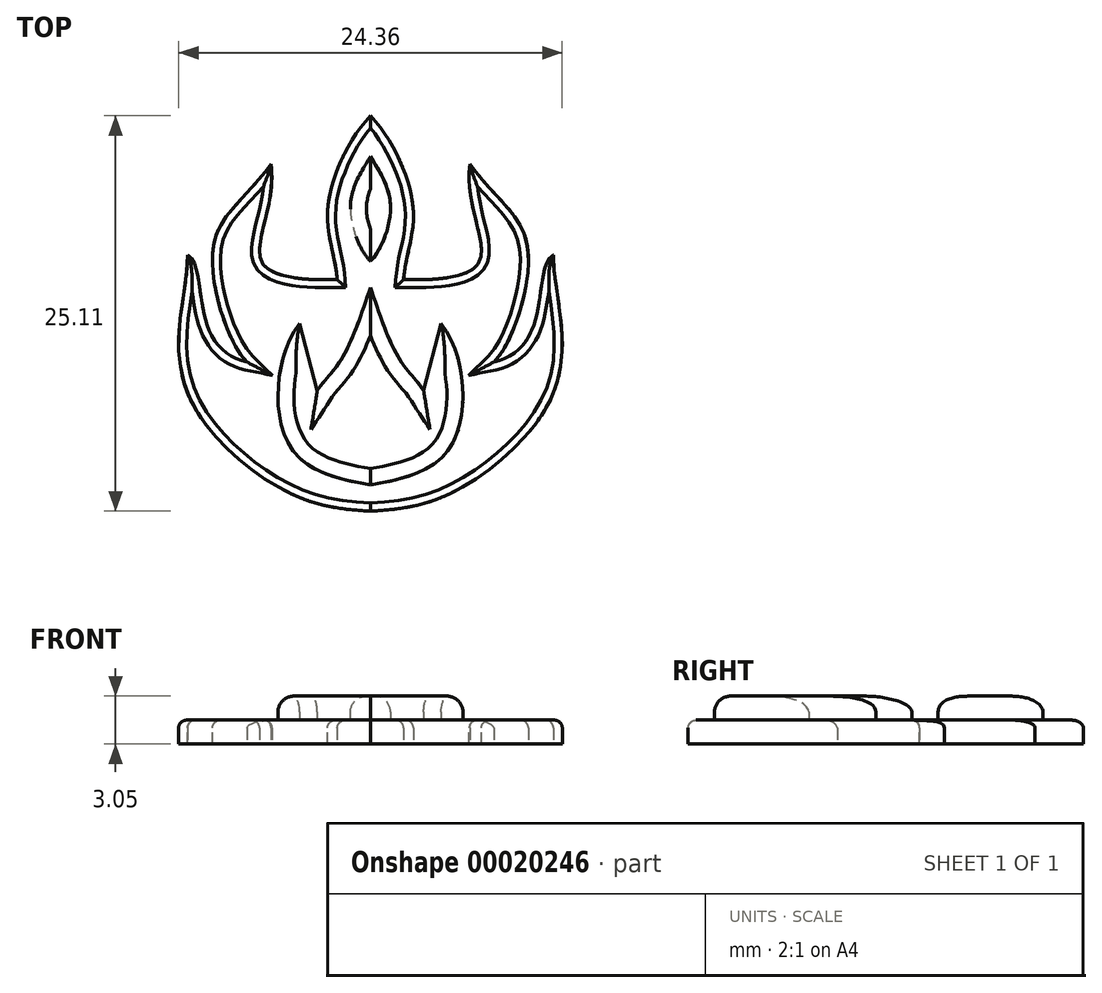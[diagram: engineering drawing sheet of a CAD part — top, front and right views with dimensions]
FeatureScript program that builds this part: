
annotation { "Feature Type Name" : "Feature", "Feature Type Description" : "" }
export const myFeature = defineFeature(function(context is Context, id is Id, definition is map)
    precondition{}
    {
        {
            var Q0;
            Q0=qCreatedBy(makeId("Top.planeOp"),FACE);
            var sketch = newSketch(context, id + "F0", { "sketchPlane" : qUnion([Q0])});
            skCircle(sketch, "E0", {"center": v(0, 0) * mm, "radius": 12.7 * mm});
            skSolve(sketch);
        }
        {
            var Q0;
            Q0=makeQuery(id+"F0.imprint","IMPRINT",FACE,{"disambiguationData":[TD([[makeQuery(id+"F0.imprint","IMPRINT",EDGE,{"derivedFrom":sQuery(id+"F0.wireOp",EDGE,"E0")}),1.0]])]});
            var Q1;
            Q1=sQuery(id+"F0.wireOp",EDGE,"E0");
            extrude(context, id + "F1", {"entities" : qUnion([Q0]), "surfaceEntities" : qUnion([Q1]), "depth" : 1.52 * mm});
        }
        {
            var Q0;
            Q0=qCreatedBy(makeId("Top.planeOp"),FACE);
            var sketch = newSketch(context, id + "F2", { "sketchPlane" : qUnion([Q0])});
            skFitSpline(sketch, "E1", {"points": [v(-6.32, 9.47) * mm, v(-9.99, 4.16) * mm, v(-7.84, -3.1) * mm], "startDerivative": vector(-11.2, -15.16) * mm, "endDerivative": vector(7.05, -6.8) * mm});
            skFitSpline(sketch, "E2", {"points": [v(0, 12.55) * mm, v(-2.72, 6.54) * mm, v(-2.1, 2.14) * mm], "startDerivative": vector(-7.74, -8.23) * mm, "endDerivative": vector(0.56, -9.4) * mm});
            skFitSpline(sketch, "E3", {"points": [v(-6.32, 9.47) * mm, v(-6.81, 3.12) * mm, v(-2.1, 2.14) * mm], "startDerivative": vector(2.17, -14.8) * mm, "endDerivative": vector(8.57, 0.21) * mm});
            skFitSpline(sketch, "E4", {"points": [v(-7.84, -3.1) * mm, v(-10.43, -0.58) * mm, v(-11.63, 3.7) * mm], "startDerivative": vector(-7.72, 1.59) * mm, "endDerivative": vector(-4.68, 1.95) * mm});
            skFitSpline(sketch, "E5", {"points": [v(-11.63, 3.7) * mm, v(-12.18, -1.7) * mm, v(-10.5, -7) * mm, v(-4.34, -11.76) * mm, v(0, -12.56) * mm], "startDerivative": vector(1.13, -13.77) * mm, "endDerivative": vector(14.52, -0.9) * mm});
            skLineSegment(sketch, "E6", {"start": v(0, 12.55) * mm, "end": v(0, 0) * mm});
            skFitSpline(sketch, "E7.MirrorCS", {"points": [v(0, 12.55) * mm, v(2.72, 6.54) * mm, v(2.1, 2.14) * mm], "startDerivative": vector(7.74, -8.23) * mm, "endDerivative": vector(-0.56, -9.4) * mm});
            skFitSpline(sketch, "E8.MirrorCS", {"points": [v(6.32, 9.47) * mm, v(6.81, 3.12) * mm, v(2.1, 2.14) * mm], "startDerivative": vector(-2.17, -14.8) * mm, "endDerivative": vector(-8.57, 0.21) * mm});
            skFitSpline(sketch, "E9.MirrorCS", {"points": [v(6.32, 9.47) * mm, v(9.99, 4.16) * mm, v(7.84, -3.1) * mm], "startDerivative": vector(11.2, -15.16) * mm, "endDerivative": vector(-7.05, -6.8) * mm});
            skFitSpline(sketch, "E10.MirrorCS", {"points": [v(11.63, 3.7) * mm, v(12.18, -1.7) * mm, v(10.5, -7) * mm, v(4.34, -11.76) * mm, v(0, -12.56) * mm], "startDerivative": vector(-1.13, -13.77) * mm, "endDerivative": vector(-14.52, -0.9) * mm});
            skFitSpline(sketch, "E11.MirrorCS", {"points": [v(7.84, -3.1) * mm, v(10.43, -0.58) * mm, v(11.63, 3.7) * mm], "startDerivative": vector(7.72, 1.59) * mm, "endDerivative": vector(4.68, 1.95) * mm});
            skLineSegment(sketch, "E12.rect.bottom", {"start": v(-14.8, 14.72) * mm, "end": v(14.8, 14.72) * mm});
            skLineSegment(sketch, "E12.rect.top", {"start": v(-14.8, -14.72) * mm, "end": v(14.8, -14.72) * mm});
            skLineSegment(sketch, "E12.rect.left", {"start": v(-14.8, 14.72) * mm, "end": v(-14.8, -14.72) * mm});
            skLineSegment(sketch, "E12.rect.right", {"start": v(14.8, 14.72) * mm, "end": v(14.8, -14.72) * mm});
            skPoint(sketch, "E12.rect.middle", {"position": v(0, 0) * mm});
            skSolve(sketch);
        }
        {
            var Q0;
            Q0 = qSketchRegion(id + "F2", true);
            var Q1;
            Q1=makeQuery(id+"F1.opExtrude","CAP_FACE",FACE,{"disambiguationData":[OSD([sQuery(id+"F0.wireOp",EDGE,"E0")])],"isStart":false});
            extrude(context, id + "F3", {"entities" : qUnion([Q0, Q1]), "operationType" : NewBodyOperationType.REMOVE, "depth" : 25.4 * mm});
        }
        {
            var Q0;
            Q0=makeQuery(id+"F1.opExtrude","CAP_FACE",FACE,{"disambiguationData":[OSD([sQuery(id+"F0.wireOp",EDGE,"E0")])],"isStart":false});
            var sketch = newSketch(context, id + "F4", { "sketchPlane" : qUnion([Q0])});
            skLineSegment(sketch, "E13", {"start": v(0, 1.65) * mm, "end": v(0, -10.9) * mm});
            skFitSpline(sketch, "E14", {"points": [v(0, -10.9) * mm, v(-4.44, -9.25) * mm, v(-5.87, -5.15) * mm, v(-4.5, -0.64) * mm], "startDerivative": vector(-14.14, 2.49) * mm, "endDerivative": vector(7.65, 9.37) * mm});
            skLineSegment(sketch, "E15", {"start": v(-4.5, -0.64) * mm, "end": v(-3.38, -4.9) * mm});
            skFitSpline(sketch, "E16", {"points": [v(-3.38, -4.9) * mm, v(-1.77, -2.8) * mm, v(0, 1.65) * mm], "startDerivative": vector(3.53, 5.42) * mm, "endDerivative": vector(2.06, 6.1) * mm});
            skFitSpline(sketch, "E17", {"points": [v(0, 9.97) * mm, v(-1.1, 7.83) * mm, v(-1.1, 5.45) * mm, v(0, 3.31) * mm], "startDerivative": vector(-3.03, -4.82) * mm, "endDerivative": vector(4.24, -4.11) * mm});
            skLineSegment(sketch, "E18.MirrorCS", {"start": v(4.5, -0.64) * mm, "end": v(3.38, -4.9) * mm});
            skFitSpline(sketch, "E19.MirrorCS", {"points": [v(3.38, -4.9) * mm, v(1.77, -2.8) * mm, v(0, 1.65) * mm], "startDerivative": vector(-3.53, 5.42) * mm, "endDerivative": vector(-2.06, 6.1) * mm});
            skFitSpline(sketch, "E20.MirrorCS", {"points": [v(0, -10.9) * mm, v(4.44, -9.25) * mm, v(5.87, -5.15) * mm, v(4.5, -0.64) * mm], "startDerivative": vector(14.14, 2.49) * mm, "endDerivative": vector(-7.65, 9.37) * mm});
            skFitSpline(sketch, "E21.MirrorCS", {"points": [v(0, 9.97) * mm, v(1.1, 7.83) * mm, v(1.1, 5.45) * mm, v(0, 3.31) * mm], "startDerivative": vector(3.03, -4.82) * mm, "endDerivative": vector(-4.24, -4.11) * mm});
            skSolve(sketch);
        }
        {
            var Q0;
            Q0 = qSketchRegion(id + "F4", true);
            extrude(context, id + "F5", {"entities" : qUnion([Q0]), "operationType" : NewBodyOperationType.ADD, "depth" : 1.52 * mm});
        }
        {
            var Q0;
            Q0=makeQuery(id+"F5.opExtrude","CAP_EDGE",EDGE,{"disambiguationData":[OSD([sQuery(id+"F4.wireOp",EDGE,"E14")])],"isStart":false});
            var Q1;
            Q1=makeQuery(id+"F5.opExtrude","CAP_FACE",FACE,{"disambiguationData":[OSD([sQuery(id+"F4.wireOp",EDGE,"E14"),sQuery(id+"F4.wireOp",EDGE,"E15"),sQuery(id+"F4.wireOp",EDGE,"E16"),sQuery(id+"F4.wireOp",EDGE,"E18.MirrorCS"),sQuery(id+"F4.wireOp",EDGE,"E19.MirrorCS"),sQuery(id+"F4.wireOp",EDGE,"E20.MirrorCS")])],"isStart":false});
            var Q2;
            Q2=makeQuery(id+"F5.opExtrude","CAP_FACE",FACE,{"disambiguationData":[OSD([sQuery(id+"F4.wireOp",EDGE,"E17"),sQuery(id+"F4.wireOp",EDGE,"E21.MirrorCS")])],"isStart":false});
            fillet(context, id + "F6", {"entities" : qUnion([Q0, Q1, Q2]), "radius" : 1.02 * mm, "tangentPropagation" : true, "allowEdgeOverflow" : false});
        }
        {
            var Q0;
            {var subQ0=sQuery(id+"F0.wireOp",EDGE,"E0");Q0=makeQuery(id+"F3.boolean.opBoolean","INTERSECT",EDGE,{"derivedFrom":[makeQuery(id+"F1.opExtrude","CAP_FACE",FACE,{"disambiguationData":[OSD([subQ0])],"isStart":false}),makeQuery(id+"F3.opExtrude","CAP_FACE",FACE,{"disambiguationData":[OSD([subQ0])],"isStart":true}),makeQuery(id+"F3.opExtrude","SWEPT_FACE",FACE,{"disambiguationData":[OSD([sQuery(id+"F2.wireOp",EDGE,"E5")])]})]});}
            var Q1;
            {var subQ0=sQuery(id+"F0.wireOp",EDGE,"E0");Q1=makeQuery(id+"F3.boolean.opBoolean","INTERSECT",EDGE,{"derivedFrom":[makeQuery(id+"F1.opExtrude","CAP_FACE",FACE,{"disambiguationData":[OSD([subQ0])],"isStart":false}),makeQuery(id+"F3.opExtrude","CAP_FACE",FACE,{"disambiguationData":[OSD([subQ0])],"isStart":true}),makeQuery(id+"F3.opExtrude","SWEPT_FACE",FACE,{"disambiguationData":[OSD([sQuery(id+"F2.wireOp",EDGE,"E10.MirrorCS")])]})]});}
            var Q2;
            {var subQ0=sQuery(id+"F0.wireOp",EDGE,"E0");Q2=makeQuery(id+"F3.boolean.opBoolean","INTERSECT",EDGE,{"derivedFrom":[makeQuery(id+"F1.opExtrude","CAP_FACE",FACE,{"disambiguationData":[OSD([subQ0])],"isStart":false}),makeQuery(id+"F3.opExtrude","CAP_FACE",FACE,{"disambiguationData":[OSD([subQ0])],"isStart":true}),makeQuery(id+"F3.opExtrude","SWEPT_FACE",FACE,{"disambiguationData":[OSD([sQuery(id+"F2.wireOp",EDGE,"E3")])]})]});}
            var Q3;
            {var subQ0=sQuery(id+"F0.wireOp",EDGE,"E0");Q3=makeQuery(id+"F3.boolean.opBoolean","INTERSECT",EDGE,{"derivedFrom":[makeQuery(id+"F1.opExtrude","CAP_FACE",FACE,{"disambiguationData":[OSD([subQ0])],"isStart":false}),makeQuery(id+"F3.opExtrude","CAP_FACE",FACE,{"disambiguationData":[OSD([subQ0])],"isStart":true}),makeQuery(id+"F3.opExtrude","SWEPT_FACE",FACE,{"disambiguationData":[OSD([sQuery(id+"F2.wireOp",EDGE,"E1")])]})]});}
            var Q4;
            {var subQ0=sQuery(id+"F0.wireOp",EDGE,"E0");Q4=makeQuery(id+"F3.boolean.opBoolean","INTERSECT",EDGE,{"derivedFrom":[makeQuery(id+"F1.opExtrude","CAP_FACE",FACE,{"disambiguationData":[OSD([subQ0])],"isStart":false}),makeQuery(id+"F3.opExtrude","CAP_FACE",FACE,{"disambiguationData":[OSD([subQ0])],"isStart":true}),makeQuery(id+"F3.opExtrude","SWEPT_FACE",FACE,{"disambiguationData":[OSD([sQuery(id+"F2.wireOp",EDGE,"E4")])]})]});}
            var Q5;
            {var subQ0=sQuery(id+"F0.wireOp",EDGE,"E0");Q5=makeQuery(id+"F3.boolean.opBoolean","INTERSECT",EDGE,{"derivedFrom":[makeQuery(id+"F1.opExtrude","CAP_FACE",FACE,{"disambiguationData":[OSD([subQ0])],"isStart":false}),makeQuery(id+"F3.opExtrude","CAP_FACE",FACE,{"disambiguationData":[OSD([subQ0])],"isStart":true}),makeQuery(id+"F3.opExtrude","SWEPT_FACE",FACE,{"disambiguationData":[OSD([sQuery(id+"F2.wireOp",EDGE,"E2")])]})]});}
            var Q6;
            {var subQ0=sQuery(id+"F0.wireOp",EDGE,"E0");Q6=makeQuery(id+"F3.boolean.opBoolean","INTERSECT",EDGE,{"derivedFrom":[makeQuery(id+"F1.opExtrude","CAP_FACE",FACE,{"disambiguationData":[OSD([subQ0])],"isStart":false}),makeQuery(id+"F3.opExtrude","CAP_FACE",FACE,{"disambiguationData":[OSD([subQ0])],"isStart":true}),makeQuery(id+"F3.opExtrude","SWEPT_FACE",FACE,{"disambiguationData":[OSD([sQuery(id+"F2.wireOp",EDGE,"E7.MirrorCS")])]})]});}
            var Q7;
            {var subQ0=sQuery(id+"F0.wireOp",EDGE,"E0");Q7=makeQuery(id+"F3.boolean.opBoolean","INTERSECT",EDGE,{"derivedFrom":[makeQuery(id+"F1.opExtrude","CAP_FACE",FACE,{"disambiguationData":[OSD([subQ0])],"isStart":false}),makeQuery(id+"F3.opExtrude","CAP_FACE",FACE,{"disambiguationData":[OSD([subQ0])],"isStart":true}),makeQuery(id+"F3.opExtrude","SWEPT_FACE",FACE,{"disambiguationData":[OSD([sQuery(id+"F2.wireOp",EDGE,"E8.MirrorCS")])]})]});}
            var Q8;
            {var subQ0=sQuery(id+"F0.wireOp",EDGE,"E0");Q8=makeQuery(id+"F3.boolean.opBoolean","INTERSECT",EDGE,{"derivedFrom":[makeQuery(id+"F1.opExtrude","CAP_FACE",FACE,{"disambiguationData":[OSD([subQ0])],"isStart":false}),makeQuery(id+"F3.opExtrude","CAP_FACE",FACE,{"disambiguationData":[OSD([subQ0])],"isStart":true}),makeQuery(id+"F3.opExtrude","SWEPT_FACE",FACE,{"disambiguationData":[OSD([sQuery(id+"F2.wireOp",EDGE,"E9.MirrorCS")])]})]});}
            var Q9;
            {var subQ0=sQuery(id+"F0.wireOp",EDGE,"E0");Q9=makeQuery(id+"F3.boolean.opBoolean","INTERSECT",EDGE,{"derivedFrom":[makeQuery(id+"F1.opExtrude","CAP_FACE",FACE,{"disambiguationData":[OSD([subQ0])],"isStart":false}),makeQuery(id+"F3.opExtrude","CAP_FACE",FACE,{"disambiguationData":[OSD([subQ0])],"isStart":true}),makeQuery(id+"F3.opExtrude","SWEPT_FACE",FACE,{"disambiguationData":[OSD([sQuery(id+"F2.wireOp",EDGE,"E11.MirrorCS")])]})]});}
            fillet(context, id + "F7", {"entities" : qUnion([Q0, Q1, Q2, Q3, Q4, Q5, Q6, Q7, Q8, Q9]), "radius" : 0.5 * mm, "tangentPropagation" : true, "allowEdgeOverflow" : false});
        }
    });
